# Revit family: KEUCO_34962010000
name_source: partatom
category: Sonderausstattung
revit_build: Autodesk Revit 2016 (Build: 20150220_1215(x64)
units: mm (PartAtom-declared; Revit-internal decimal feet)

## family parameters
Arbeitsebenenbasiert = Nein
Beim Laden mit Abzugskörper schneiden = Nein
Bemaßung runder Anschluss = Durchmesser verwenden
Gemeinsam genutzt = Nein
Immer vertikal = Ja
Raumberechnungspunkt = Nein
Teiletyp = Normal

## types (2) — shared parameters
Beschreibung = zur Montage an Winkelgriffen
Gewicht = 382
Hersteller = KEUCO
Kategorie = ACC
Preisgruppe = 1
Serie = Plan
URL = https://www.keuco.com
Verwendung = CA / GWC / WC

## per-type parameters (varying)
| type | Ausschreibungstext |
| 34962010000 | KEUCO PLAN CARE Toilettenpapierhalter 34962010000 
hochglanzverchromt zur nachträglichen Montage an 
Haltegriffen 34901…, Winkelgriffen 34906…., 34907…, 
und Stützklappgriffe 32302….
Höhe Mitte Haltegriff bis Unterkante Papierrollenhalter 125 mm |
| 34962170000 | KEUCO PLAN CARE Toilettenpapierhalter 34962170000 
Aluminium silber-eloxiert (E6 EV1)/verchromt
zur nachträglichen Montage an 
Haltegriffen 34901…, Winkelgriffen 34906…., 34907…, 
und Stützklappgriffe 32302….
Höhe Mitte Haltegriff bis Unterkante Papierrollenhalter 125 mm |

note: column(s) folded — value = type name in every type: Artikelnummer

## geometry (parser evidence)
native form markers: Blend x4, Sweep x2
no freeform markers — native parametric forms only
